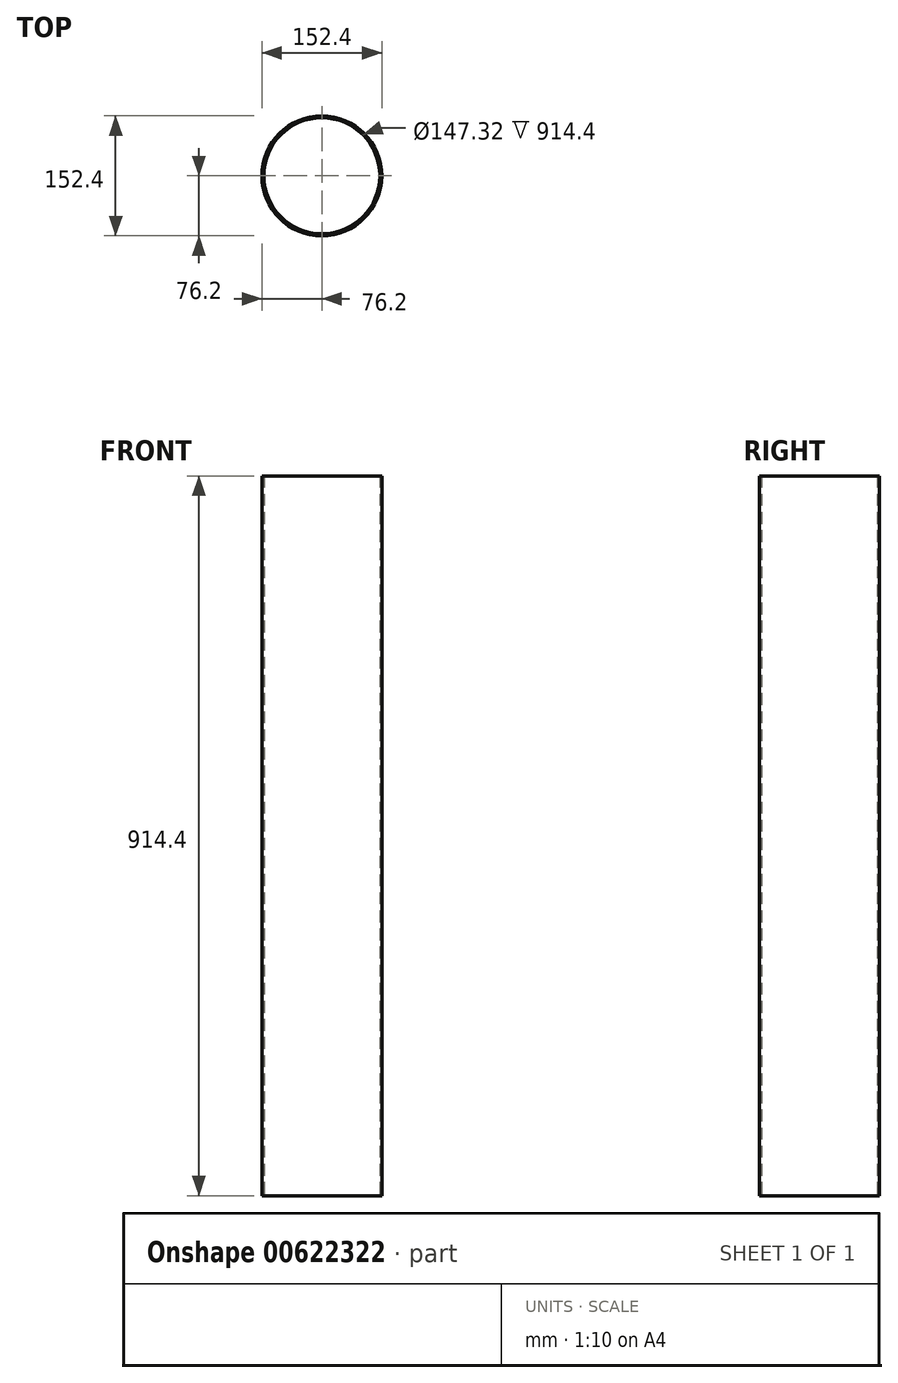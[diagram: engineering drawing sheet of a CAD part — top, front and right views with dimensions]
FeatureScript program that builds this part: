
annotation { "Feature Type Name" : "Feature", "Feature Type Description" : "" }
export const myFeature = defineFeature(function(context is Context, id is Id, definition is map)
    precondition{}
    {
        {
            var Q0;
            Q0=qCreatedBy(makeId("Top.planeOp"),FACE);
            var sketch = newSketch(context, id + "F0", { "sketchPlane" : qUnion([Q0])});
            skCircle(sketch, "E0", {"center": v(0, 0) * mm, "radius": 76.2 * mm});
            skCircle(sketch, "E1", {"center": v(0, 0) * mm, "radius": 73.66 * mm});
            skSolve(sketch);
        }
        {
            var Q0;
            Q0 = qSketchRegion(id + "F0", true);
            extrude(context, id + "F1", {"entities" : qUnion([Q0]), "depth" : 914.4 * mm, "offsetDistance" : 25.4 * mm});
        }
    });
